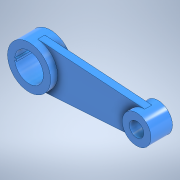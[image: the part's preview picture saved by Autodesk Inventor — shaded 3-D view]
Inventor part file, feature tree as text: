
AUTODESK INVENTOR PART (.ipt)
format: ipt  version: 2021 (Build 250183000, 183)  size: 147,968 bytes
history: native  units: mm
features: extrude x3, sketch x3, other x1
ambient origin geometry x8: Origin, YZ Plane, XZ Plane, XY Plane, X Axis, Y Axis, Z Axis, Center Point
bodies: Body1 (feature_tree)
feature tree (7):
  other  "Sólido1"
  extrude  "Extrusão1"  Depth=24.0mm
  extrude  "Extrusão2"  Depth=8.0mm
  extrude  "Extrusão3"  Depth=4.0mm TaperAngle=0.0deg
  sketch  "Esboço1"  dims[d0=16.0mm d1=24.0mm]
  sketch  "Esboço2"  dims[d2=16.0mm d3=8.0mm]
  sketch  "Esboço3"  dims[d4=60.0mm d5=4.0mm d6=0.0mm d7=12.0mm d8=0.0mm d9=1.2mm d10=0.6mm d11=1.2mm d12=0.6mm d13=12.0mm d14=0.0mm]
